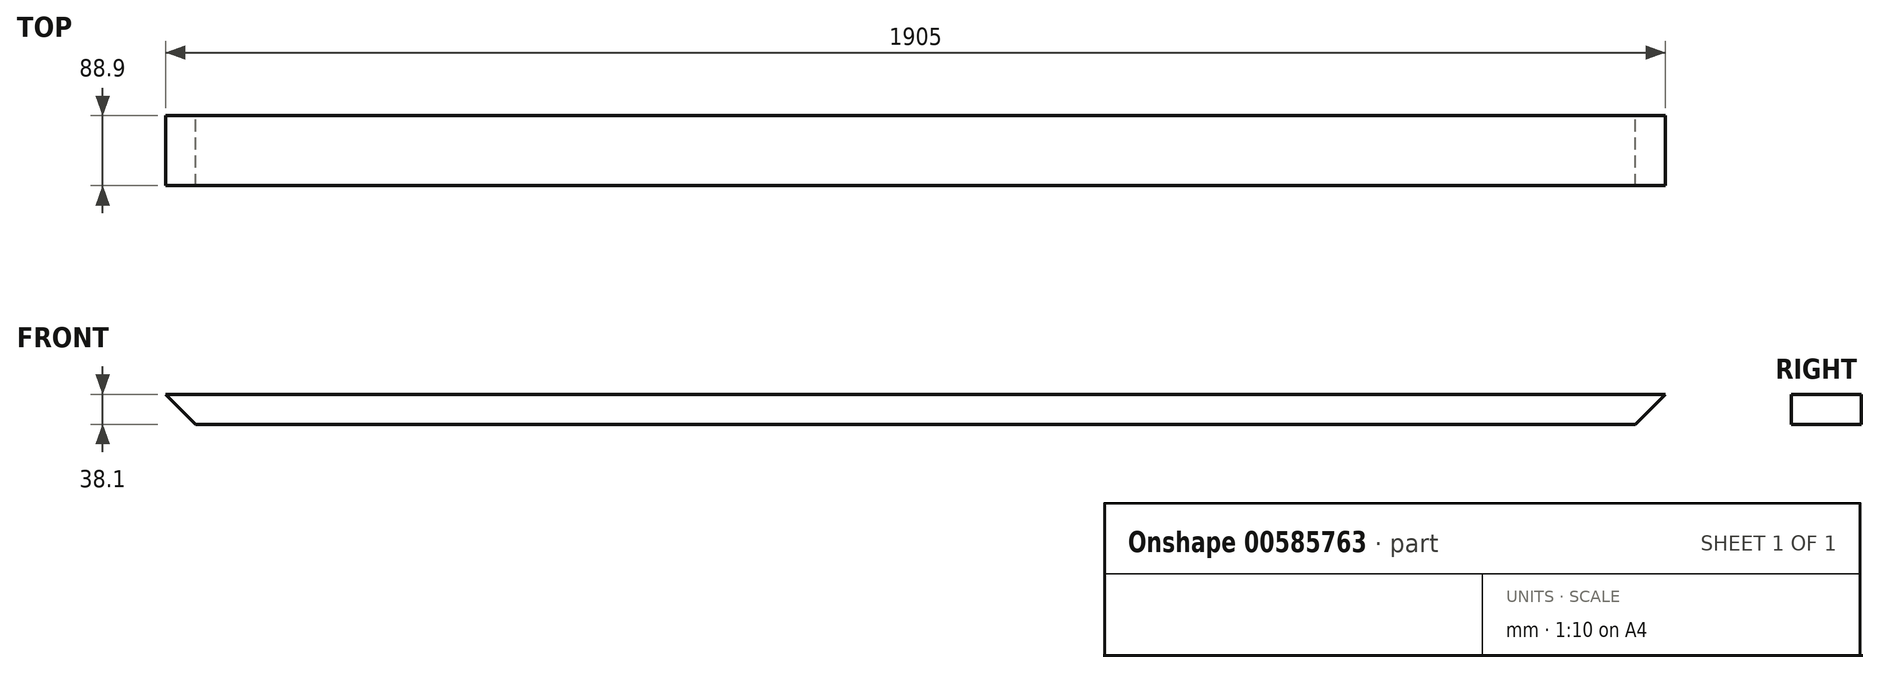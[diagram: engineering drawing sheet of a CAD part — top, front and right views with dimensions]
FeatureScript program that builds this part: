
annotation { "Feature Type Name" : "Feature", "Feature Type Description" : "" }
export const myFeature = defineFeature(function(context is Context, id is Id, definition is map)
    precondition{}
    {
        {
            var Q0;
            Q0=qCreatedBy(makeId("Front.planeOp"),FACE);
            var sketch = newSketch(context, id + "F0", { "sketchPlane" : qUnion([Q0])});
            skLineSegment(sketch, "E0", {"start": v(644.57, 0) * mm, "end": v(-1260.43, 0) * mm});
            skLineSegment(sketch, "E1", {"start": v(-1222.33, -38.1) * mm, "end": v(606.47, -38.1) * mm});
            skLineSegment(sketch, "E2", {"start": v(606.47, -38.1) * mm, "end": v(644.57, 0) * mm});
            skLineSegment(sketch, "E3", {"start": v(-1222.33, -38.1) * mm, "end": v(-1260.43, 0) * mm});
            skSolve(sketch);
        }
        {
            var Q0;
            Q0=qSketchRegion(id+"F0",true);
            extrude(context, id + "F1", {"entities" : qUnion([Q0]), "depth" : 88.9 * mm, "offsetDistance" : 25.4 * mm});
        }
    });
